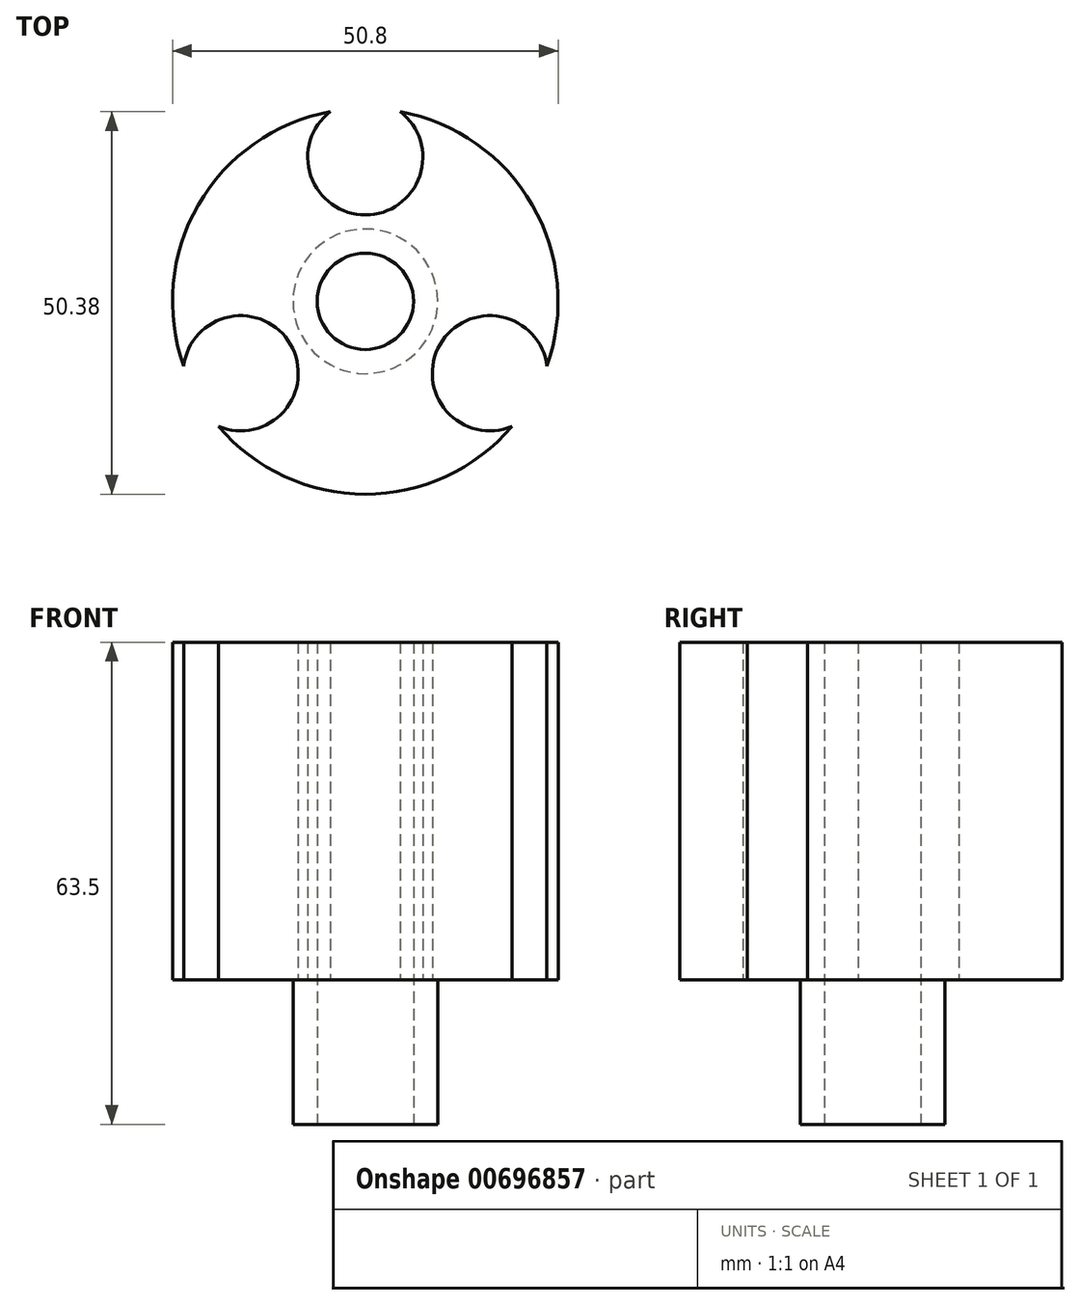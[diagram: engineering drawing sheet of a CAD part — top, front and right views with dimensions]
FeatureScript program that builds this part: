
annotation { "Feature Type Name" : "Feature", "Feature Type Description" : "" }
export const myFeature = defineFeature(function(context is Context, id is Id, definition is map)
    precondition{}
    {
        {
            var Q0;
            Q0=qCreatedBy(makeId("Top.planeOp"),FACE);
            var sketch = newSketch(context, id + "F0", { "sketchPlane" : qUnion([Q0])});
            skCircle(sketch, "E0", {"center": v(0, 0) * mm, "radius": 25.4 * mm});
            skSolve(sketch);
        }
        {
            var Q0;
            Q0 = qSketchRegion(id + "F0", true);
            extrude(context, id + "F1", {"entities" : qUnion([Q0]), "depth" : 44.45 * mm, "offsetDistance" : 25.4 * mm});
        }
        {
            var Q0;
            Q0=qCreatedBy(makeId("Top.planeOp"),FACE);
            var sketch = newSketch(context, id + "F2", { "sketchPlane" : qUnion([Q0])});
            skCircle(sketch, "E1", {"center": v(0, 0) * mm, "radius": 9.53 * mm});
            skSolve(sketch);
        }
        {
            var Q0;
            Q0 = qSketchRegion(id + "F2", true);
            extrude(context, id + "F3", {"entities" : qUnion([Q0]), "operationType" : NewBodyOperationType.ADD, "oppositeDirection" : true, "depth" : 19.05 * mm, "offsetDistance" : 25.4 * mm});
        }
        {
            var Q0;
            Q0=makeQuery(id+"F3.opExtrude","CAP_FACE",FACE,{"disambiguationData":[OSD([sQuery(id+"F2.wireOp",EDGE,"E1")])],"isStart":false});
            var sketch = newSketch(context, id + "F4", { "sketchPlane" : qUnion([Q0])});
            skCircle(sketch, "E2", {"center": v(0, 0) * mm, "radius": 6.35 * mm});
            skSolve(sketch);
        }
        {
            var Q0;
            Q0=makeQuery(id+"F4.imprint","IMPRINT",FACE,{"disambiguationData":[TD([[makeQuery(id+"F4.imprint","IMPRINT",EDGE,{"derivedFrom":sQuery(id+"F4.wireOp",EDGE,"E2")}),1.0]])]});
            var Q1;
            Q1=sQuery(id+"F4.wireOp",EDGE,"E2");
            extrude(context, id + "F5", {"entities" : qUnion([Q0]), "operationType" : NewBodyOperationType.REMOVE, "surfaceEntities" : qUnion([Q1]), "oppositeDirection" : true, "depth" : 76.2 * mm, "offsetDistance" : 25.4 * mm});
        }
        {
            var Q0;
            Q0=qCreatedBy(makeId("Top.planeOp"),FACE);
            var sketch = newSketch(context, id + "F6", { "sketchPlane" : qUnion([Q0])});
            skCircle(sketch, "E3", {"center": v(0, 18.95) * mm, "radius": 7.58 * mm});
            skCircle(sketch, "E4.1.0", {"center": v(-16.41, -9.47) * mm, "radius": 7.58 * mm});
            skCircle(sketch, "E4.2.0", {"center": v(16.41, -9.47) * mm, "radius": 7.58 * mm});
            skPoint(sketch, "E4.center", {"position": v(0, 0) * mm});
            skSolve(sketch);
        }
        {
            var Q0;
            Q0 = qSketchRegion(id + "F6", true);
            extrude(context, id + "F7", {"entities" : qUnion([Q0]), "operationType" : NewBodyOperationType.REMOVE, "depth" : 44.45 * mm, "offsetDistance" : 25.4 * mm});
        }
    });
